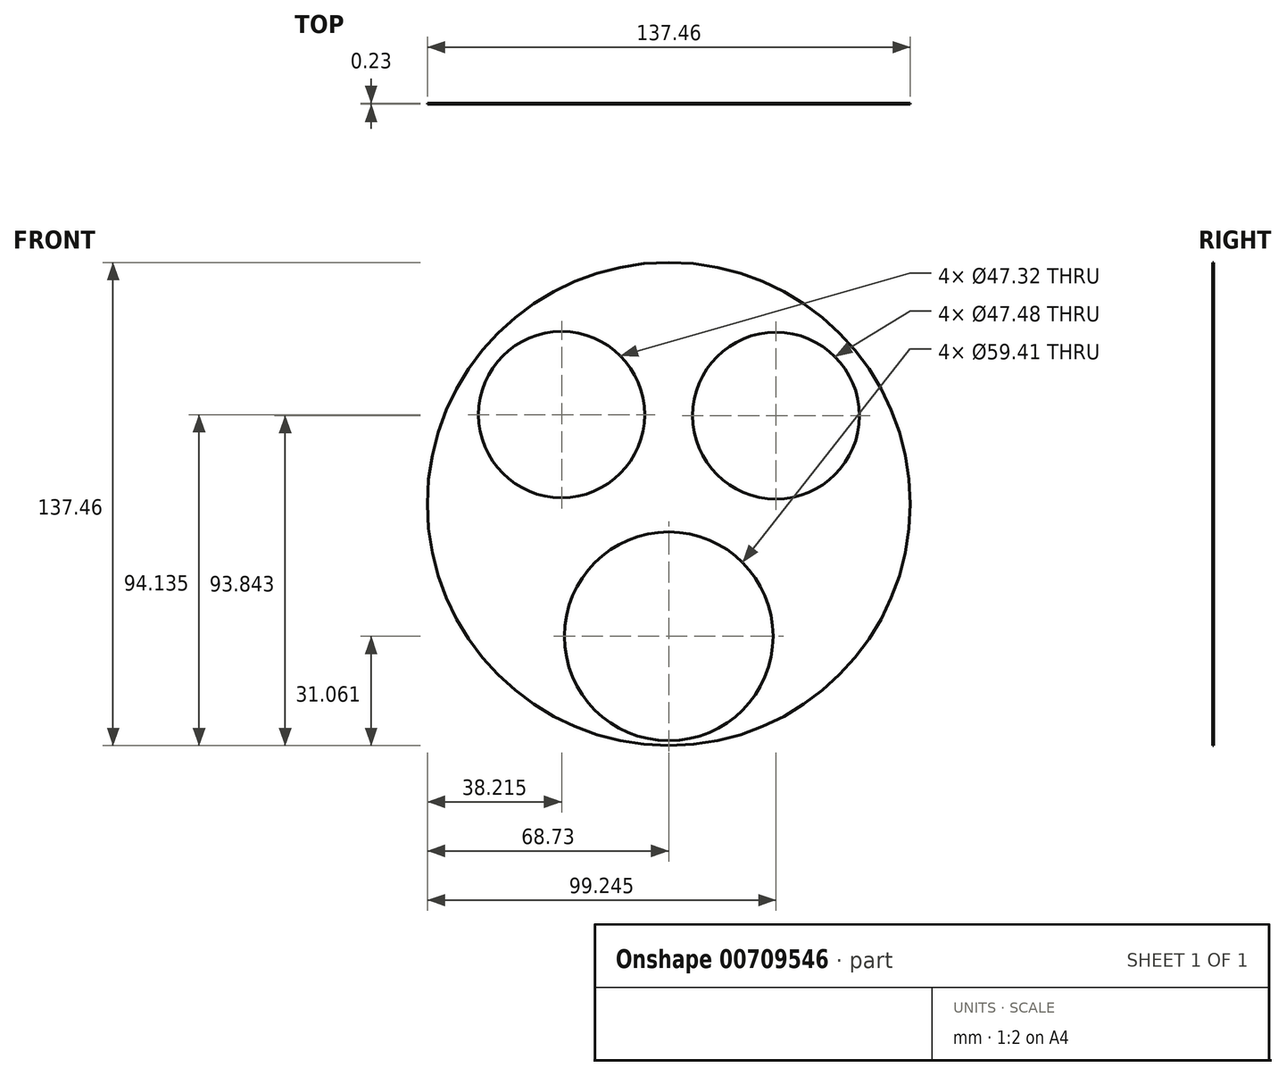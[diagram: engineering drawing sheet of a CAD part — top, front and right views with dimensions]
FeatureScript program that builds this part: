
annotation { "Feature Type Name" : "Feature", "Feature Type Description" : "" }
export const myFeature = defineFeature(function(context is Context, id is Id, definition is map)
    precondition{}
    {
        {
            var Q0;
            Q0=qCreatedBy(makeId("Front.planeOp"),FACE);
            var sketch = newSketch(context, id + "F0", { "sketchPlane" : qUnion([Q0])});
            skCircle(sketch, "E0", {"center": v(0, 3.65) * mm, "radius": 68.73 * mm});
            skCircle(sketch, "E1", {"center": v(-30.51, 29.05) * mm, "radius": 23.66 * mm});
            skCircle(sketch, "E2", {"center": v(30.51, 28.76) * mm, "radius": 23.74 * mm});
            skCircle(sketch, "E3", {"center": v(0, -34.02) * mm, "radius": 29.7 * mm});
            skSolve(sketch);
        }
        {
            var Q0;
            Q0 = qSketchRegion(id + "F0", true);
            extrude(context, id + "F1", {"entities" : qUnion([Q0]), "depth" : .23 * mm, "offsetDistance" : 25.4 * mm});
        }
    });
